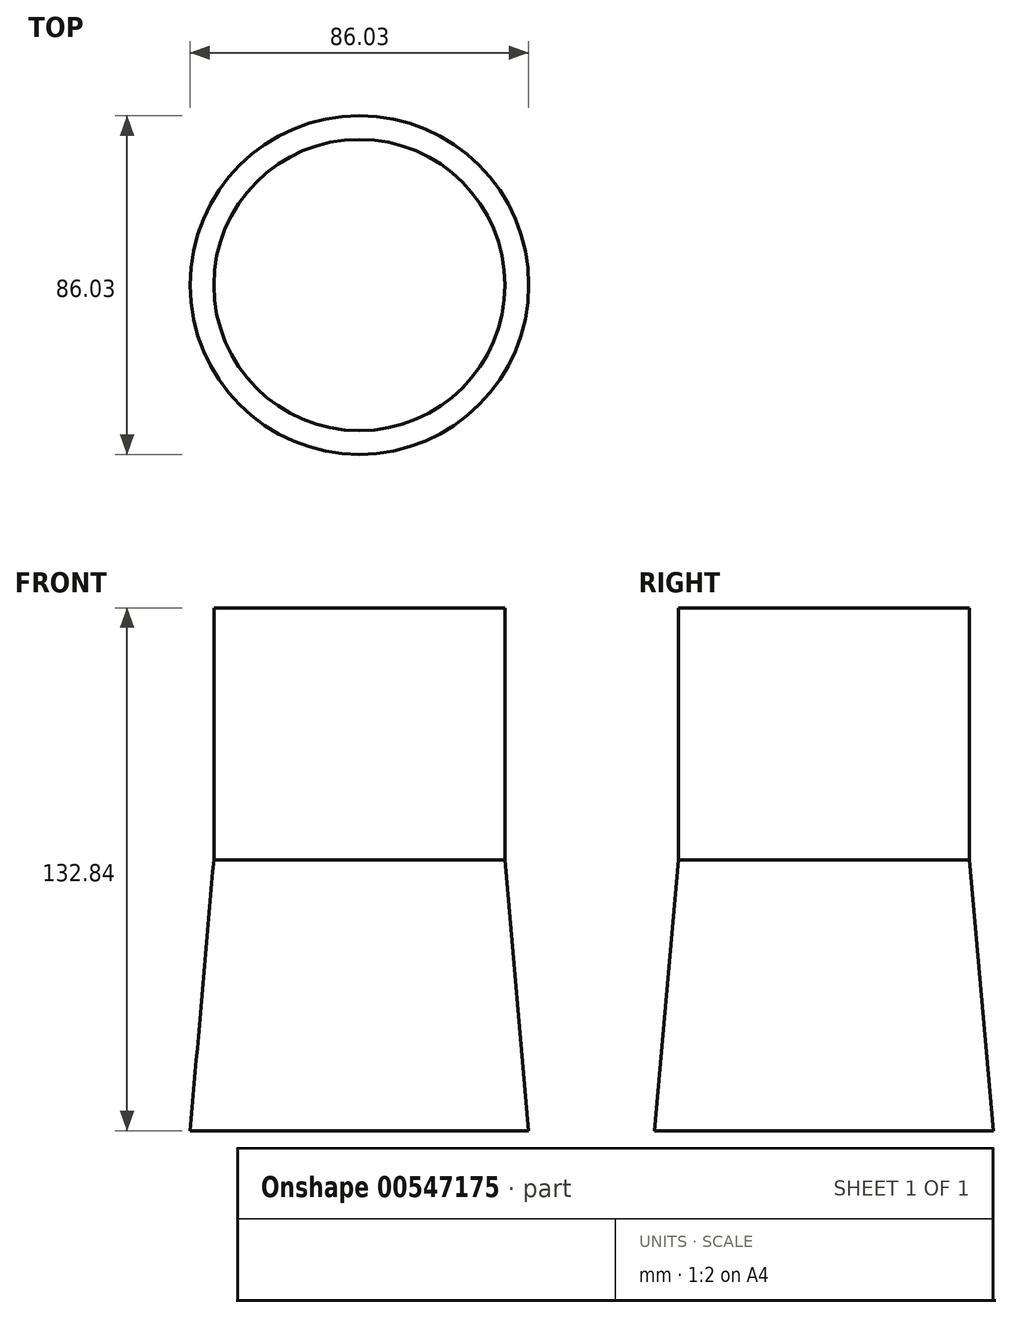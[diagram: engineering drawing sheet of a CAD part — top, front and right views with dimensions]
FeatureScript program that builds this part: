
annotation { "Feature Type Name" : "Feature", "Feature Type Description" : "" }
export const myFeature = defineFeature(function(context is Context, id is Id, definition is map)
    precondition{}
    {
        {
            var Q0;
            Q0=qCreatedBy(makeId("Top.planeOp"),FACE);
            var sketch = newSketch(context, id + "F0", { "sketchPlane" : qUnion([Q0])});
            skCircle(sketch, "E0", {"center": v(-109.3, 27.05) * mm, "radius": 37 * mm});
            skSolve(sketch);
        }
        {
            var Q0;
            Q0=makeQuery(id+"F0.imprint","IMPRINT",FACE,{"disambiguationData":[TD([[makeQuery(id+"F0.imprint","IMPRINT",EDGE,{"derivedFrom":sQuery(id+"F0.wireOp",EDGE,"E0")}),1.0]])]});
            extrude(context, id + "F1", {"entities" : qUnion([Q0]), "oppositeDirection" : true, "depth" : 68.83 * mm, "offsetDistance" : 25.4 * mm, "hasDraft" : true, "draftAngle" : 5 * degree, "hasSecondDirection" : true, "secondDirectionOppositeDirection" : false, "secondDirectionDepth" : 64 * mm});
        }
    });
